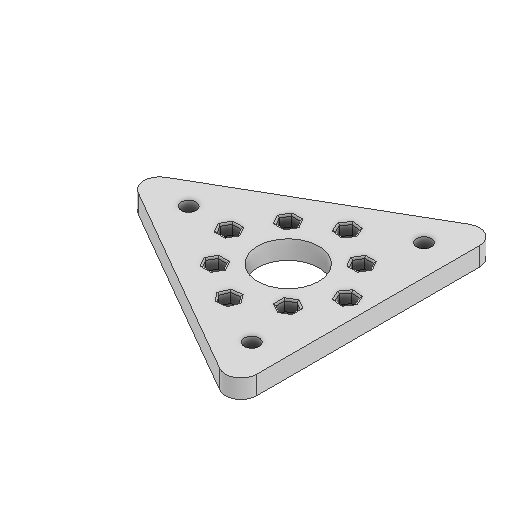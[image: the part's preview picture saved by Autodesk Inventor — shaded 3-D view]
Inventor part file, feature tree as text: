
AUTODESK INVENTOR PART (.ipt)
format: ipt  version: 2025.1 (Build 291241020, 241B)  size: 416,768 bytes
history: native  units: in
note: dims shown in document units (in); Inventor stores cm internally (conversion verified against a paired STEP export)
features: sketch x4, extrude x3, fillet x2
ambient origin geometry x8: Origin, YZ Plane, XZ Plane, XY Plane, X Axis, Y Axis, Z Axis, Center Point
bodies: Solid1 (feature_tree)
feature tree (9):
  extrude  "Extrusion1"  Depth=4.0415in
  fillet  "Fillet1"  Radius=4.0415in
  sketch  "Sketch3"  dims[d5=120.0deg d6=120.0deg d7=0.4724in d8=0.0in]
  extrude  "Extrusion2"  Depth=0.481in
  extrude  "Extrusion3"  TaperAngle=120.0deg  [1 undecoded]
  fillet  "Fillet2"  Radius=0.4724in
  sketch  "Sketch Circular Pattern1"  dims[d0=7.0in d1=1.5472in d2=4.0415in]
  sketch  "Sketch Circular Pattern2"  dims[d3=2.5161in d4=0.481in]
  sketch  "Sketch Circular Pattern3"  dims[d9=0.3937in d11=0.0203in d13=7.874in d15=360.0deg d17=1.1811in d19=360.0deg d21=0.2244in d22=0.2244in d23=1.8559in d24=1.8559in d25=0.928in d26=0.928in d27=0.2244in d35=0.3937in d36=0.0in d41=0.3937in d47=0.2756in d48=0.0in d49=0.0394in d51=1.4961in d52=1.4961in d53=1.4961in d54=1.4961in d55=0.377in d56=2.5161in d57=1.1811in d59=360.0deg]
note: 1 required parameter value undecoded (feature->parameter linkage not recoverable at this tier; creation-order binding heuristic only, values carry confidence <= 0.55)
